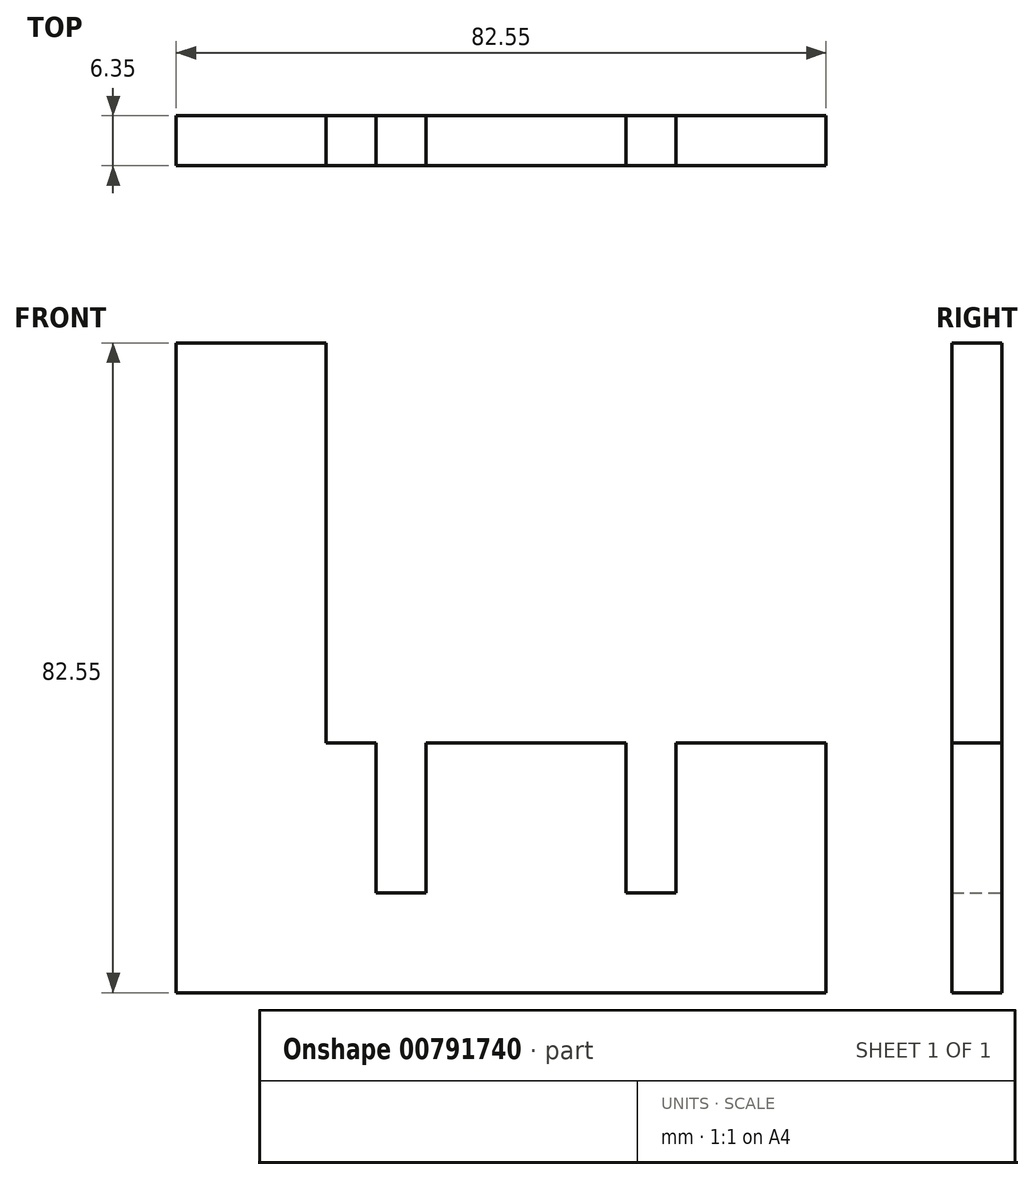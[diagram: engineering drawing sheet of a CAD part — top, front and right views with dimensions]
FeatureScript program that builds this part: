
annotation { "Feature Type Name" : "Feature", "Feature Type Description" : "" }
export const myFeature = defineFeature(function(context is Context, id is Id, definition is map)
    precondition{}
    {
        {
            var Q0;
            Q0=qCreatedBy(makeId("Front.planeOp"),FACE);
            var sketch = newSketch(context, id + "F0", { "sketchPlane" : qUnion([Q0])});
            skLineSegment(sketch, "E0.bottom", {"start": v(0, 0) * mm, "end": v(82.55, 0) * mm});
            skLineSegment(sketch, "E0.top", {"start": v(0, 82.55) * mm, "end": v(19.05, 82.55) * mm});
            skLineSegment(sketch, "E0.left", {"start": v(0, 0) * mm, "end": v(0, 82.55) * mm});
            skLineSegment(sketch, "E0.right", {"start": v(82.55, 0) * mm, "end": v(82.55, 31.75) * mm});
            skLineSegment(sketch, "E1.top", {"start": v(82.55, 31.75) * mm, "end": v(63.5, 31.75) * mm});
            skLineSegment(sketch, "E1.right", {"start": v(19.05, 82.55) * mm, "end": v(19.05, 31.75) * mm});
            skLineSegment(sketch, "E2.top", {"start": v(25.4, 12.7) * mm, "end": v(31.75, 12.7) * mm});
            skLineSegment(sketch, "E2.left", {"start": v(25.4, 31.75) * mm, "end": v(25.4, 12.7) * mm});
            skLineSegment(sketch, "E2.right", {"start": v(31.75, 31.75) * mm, "end": v(31.75, 12.7) * mm});
            skLineSegment(sketch, "E3.top", {"start": v(57.15, 12.7) * mm, "end": v(63.5, 12.7) * mm});
            skLineSegment(sketch, "E3.left", {"start": v(57.15, 31.75) * mm, "end": v(57.15, 12.7) * mm});
            skLineSegment(sketch, "E3.right", {"start": v(63.5, 31.75) * mm, "end": v(63.5, 12.7) * mm});
            skLineSegment(sketch, "E4.trimOffspring", {"start": v(25.4, 31.75) * mm, "end": v(19.05, 31.75) * mm});
            skLineSegment(sketch, "E5.trimOffspring", {"start": v(57.15, 31.75) * mm, "end": v(31.75, 31.75) * mm});
            skSolve(sketch);
        }
        {
            var Q0;
            Q0=qSketchRegion(id+"F0",true);
            extrude(context, id + "F1", {"entities" : qUnion([Q0]), "depth" : 6.35 * mm, "offsetDistance" : 25.4 * mm});
        }
    });
